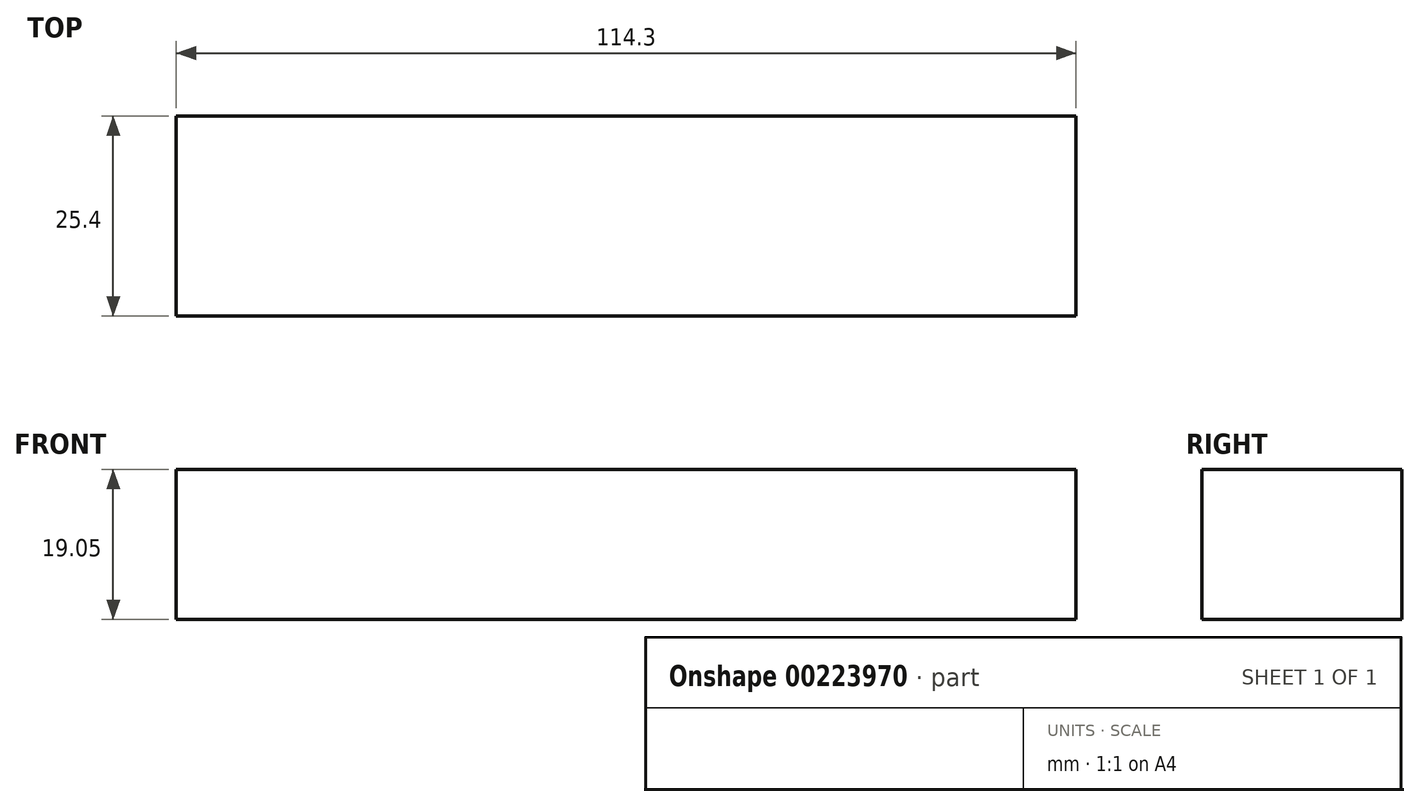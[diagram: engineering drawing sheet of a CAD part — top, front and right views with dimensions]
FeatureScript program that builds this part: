
annotation { "Feature Type Name" : "Feature", "Feature Type Description" : "" }
export const myFeature = defineFeature(function(context is Context, id is Id, definition is map)
    precondition{}
    {
        {
            var Q0;
            Q0=qCreatedBy(makeId("Front.planeOp"),FACE);
            var sketch = newSketch(context, id + "F0", { "sketchPlane" : qUnion([Q0])});
            skLineSegment(sketch, "E0.bottom", {"start": v(56.63, 27.84) * mm, "end": v(-57.67, 27.84) * mm});
            skLineSegment(sketch, "E0.top", {"start": v(56.63, 46.9) * mm, "end": v(-57.67, 46.9) * mm});
            skLineSegment(sketch, "E0.left", {"start": v(56.63, 27.84) * mm, "end": v(56.63, 46.9) * mm});
            skLineSegment(sketch, "E0.right", {"start": v(-57.67, 27.84) * mm, "end": v(-57.67, 46.9) * mm});
            skPoint(sketch, "E0.middle", {"position": v(-0.52, 37.37) * mm});
            skSolve(sketch);
        }
        {
            var Q0;
            Q0=makeQuery(id+"F0.imprint","IMPRINT",FACE,{"disambiguationData":[TD([[makeQuery(id+"F0.imprint","IMPRINT",EDGE,{"derivedFrom":sQuery(id+"F0.wireOp",EDGE,"E0.bottom")}),-1.0]])]});
            extrude(context, id + "F1", {"entities" : qUnion([Q0]), "endBound" : BoundingType.SYMMETRIC, "depth" : 25.4 * mm});
        }
    });
